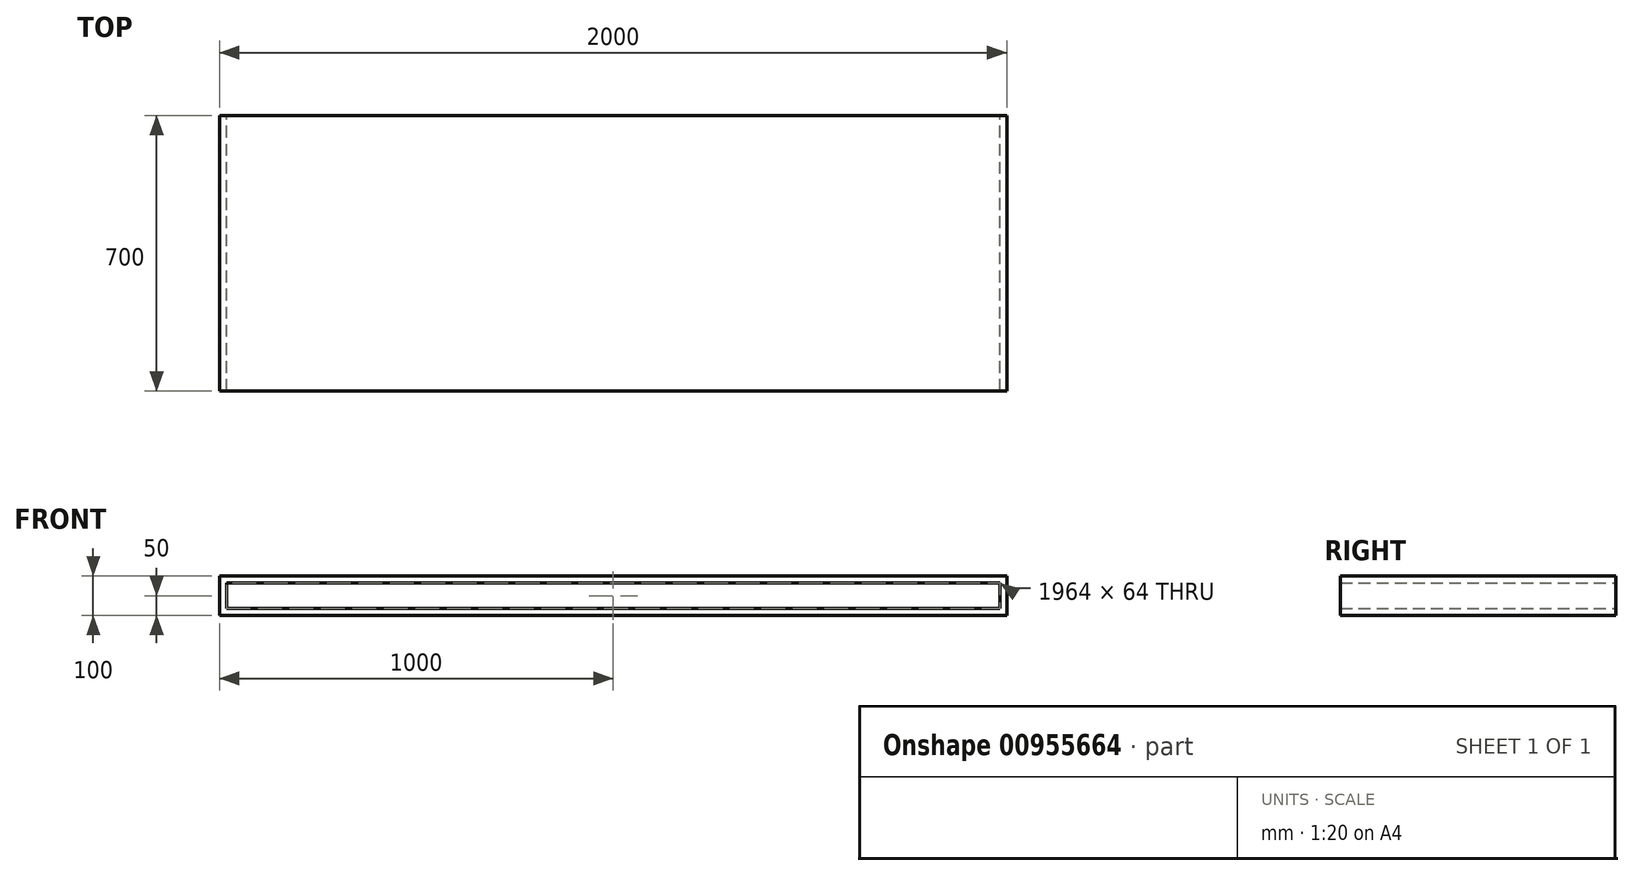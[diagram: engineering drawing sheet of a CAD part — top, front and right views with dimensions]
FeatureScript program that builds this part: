
annotation { "Feature Type Name" : "Feature", "Feature Type Description" : "" }
export const myFeature = defineFeature(function(context is Context, id is Id, definition is map)
    precondition{}
    {
        {
            var Q0;
            Q0=qCreatedBy(makeId("Front.planeOp"),FACE);
            var sketch = newSketch(context, id + "F0", { "sketchPlane" : qUnion([Q0])});
            skLineSegment(sketch, "E0.bottom", {"start": v(-1000, 0) * mm, "end": v(1000, 0) * mm});
            skLineSegment(sketch, "E0.top", {"start": v(-1000, 100) * mm, "end": v(1000, 100) * mm});
            skLineSegment(sketch, "E0.left", {"start": v(-1000, 0) * mm, "end": v(-1000, 100) * mm});
            skLineSegment(sketch, "E0.right", {"start": v(1000, 0) * mm, "end": v(1000, 100) * mm});
            skLineSegment(sketch, "E1.bottom", {"start": v(982, 82) * mm, "end": v(-982, 82) * mm});
            skLineSegment(sketch, "E1.top", {"start": v(982, 18) * mm, "end": v(-982, 18) * mm});
            skLineSegment(sketch, "E1.left", {"start": v(982, 82) * mm, "end": v(982, 18) * mm});
            skLineSegment(sketch, "E1.right", {"start": v(-982, 82) * mm, "end": v(-982, 18) * mm});
            skSolve(sketch);
        }
        {
            var Q0;
            Q0 = qSketchRegion(id + "F0", true);
            extrude(context, id + "F1", {"entities" : qUnion([Q0]), "endBound" : BoundingType.SYMMETRIC, "depth" : 700 * mm, "offsetDistance" : 25 * mm});
        }
    });
